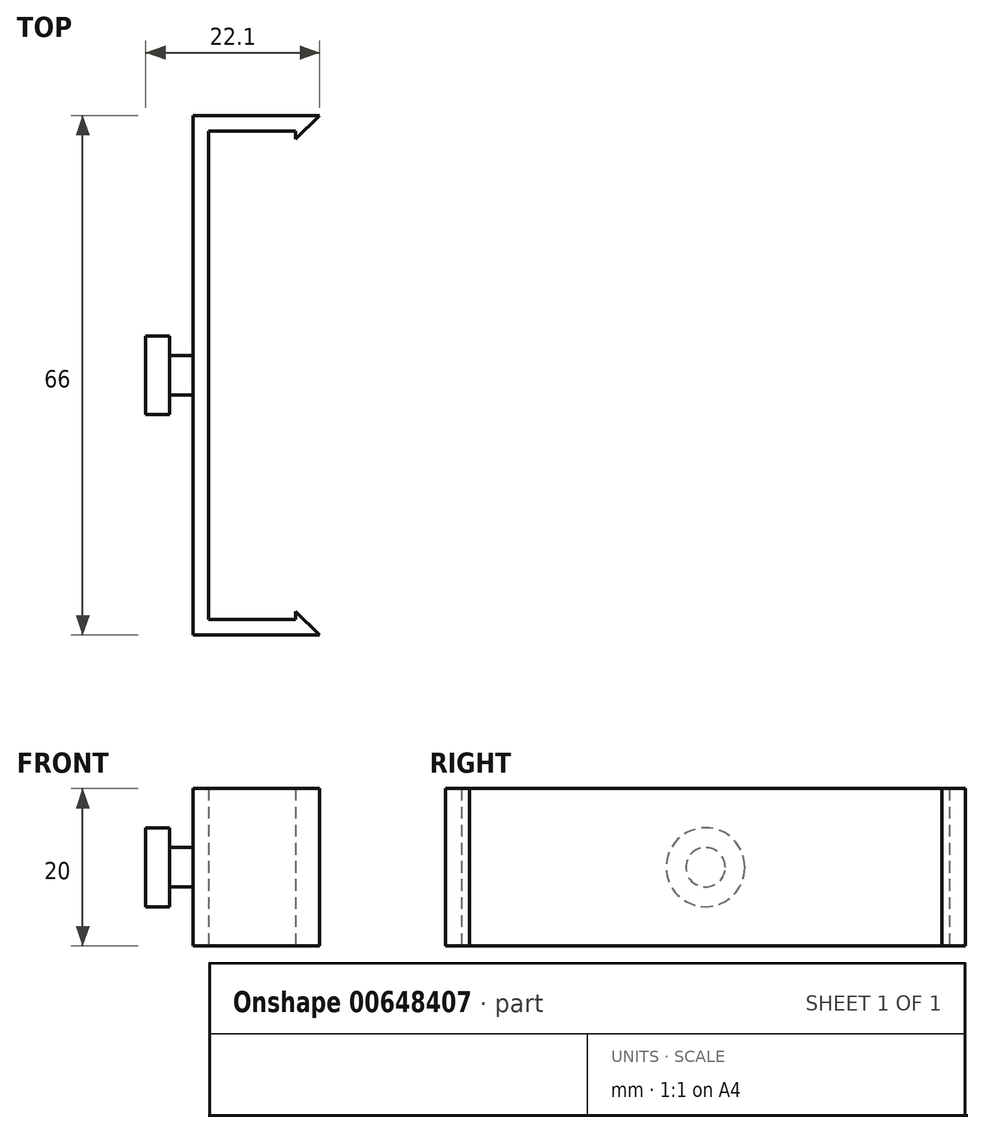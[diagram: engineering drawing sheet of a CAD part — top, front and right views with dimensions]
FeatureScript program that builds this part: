
annotation { "Feature Type Name" : "Feature", "Feature Type Description" : "" }
export const myFeature = defineFeature(function(context is Context, id is Id, definition is map)
    precondition{}
    {
        {
            var Q0;
            Q0=qCreatedBy(makeId("Top.planeOp"),FACE);
            var sketch = newSketch(context, id + "F0", { "sketchPlane" : qUnion([Q0])});
            skLineSegment(sketch, "E0", {"start": v(0.96, 0) * mm, "end": v(0.96, -33) * mm});
            skLineSegment(sketch, "E1", {"start": v(0.96, -33) * mm, "end": v(17.06, -33) * mm});
            skLineSegment(sketch, "E2", {"start": v(17.06, -33) * mm, "end": v(13.96, -30) * mm});
            skLineSegment(sketch, "E3", {"start": v(13.96, -30) * mm, "end": v(13.96, -31) * mm});
            skLineSegment(sketch, "E4", {"start": v(13.96, -31) * mm, "end": v(2.96, -31) * mm});
            skLineSegment(sketch, "E5", {"start": v(2.96, -31) * mm, "end": v(2.96, 0) * mm});
            skPoint(sketch, "E6.start.orphan", {"position": v(17.06, 48.33) * mm});
            skPoint(sketch, "E7.start.orphan", {"position": v(13.96, 44.52) * mm});
            skLineSegment(sketch, "E8.MirrorCS", {"start": v(13.96, 30) * mm, "end": v(13.96, 31) * mm});
            skLineSegment(sketch, "E9.MirrorCS", {"start": v(17.06, 33) * mm, "end": v(13.96, 30) * mm});
            skLineSegment(sketch, "E10.MirrorCS", {"start": v(13.96, 31) * mm, "end": v(2.96, 31) * mm});
            skLineSegment(sketch, "E11.MirrorCS", {"start": v(0.96, 33) * mm, "end": v(17.06, 33) * mm});
            skLineSegment(sketch, "E12.MirrorCS", {"start": v(0.96, 0) * mm, "end": v(0.96, 33) * mm});
            skLineSegment(sketch, "E13.MirrorCS", {"start": v(2.96, 31) * mm, "end": v(2.96, 0) * mm});
            skSolve(sketch);
        }
        {
            var Q0;
            Q0 = qSketchRegion(id + "F0", true);
            extrude(context, id + "F1", {"entities" : qUnion([Q0]), "depth" : 20 * mm, "offsetDistance" : 25 * mm});
        }
        {
            var Q0;
            Q0=makeQuery(id+"F1.opExtrude","SWEPT_FACE",FACE,{"disambiguationData":[OSD([sQuery(id+"F0.wireOp",EDGE,"E0"),sQuery(id+"F0.wireOp",EDGE,"E12.MirrorCS")])]});
            var sketch = newSketch(context, id + "F2", { "sketchPlane" : qUnion([Q0])});
            skLineSegment(sketch, "E14", {"start": v(0, 20) * mm, "end": v(0, 0) * mm});
            skLineSegment(sketch, "E15", {"start": v(-33, 10) * mm, "end": v(33, 10) * mm});
            skCircle(sketch, "E16", {"center": v(0, 10) * mm, "radius": 2.5 * mm});
            skSolve(sketch);
        }
        {
            var Q0;
            Q0 = qSketchRegion(id + "F2", true);
            extrude(context, id + "F3", {"entities" : qUnion([Q0]), "operationType" : NewBodyOperationType.ADD, "depth" : 3 * mm, "offsetDistance" : 25 * mm});
        }
        {
            var Q0;
            Q0=makeQuery(id+"F3.opExtrude","CAP_FACE",FACE,{"disambiguationData":[OSD([sQuery(id+"F2.wireOp",EDGE,"E16")])],"isStart":false});
            var sketch = newSketch(context, id + "F4", { "sketchPlane" : qUnion([Q0])});
            skCircle(sketch, "E17", {"center": v(0, 10) * mm, "radius": 5 * mm});
            skSolve(sketch);
        }
        {
            var Q0;
            Q0 = qSketchRegion(id + "F4", true);
            extrude(context, id + "F5", {"entities" : qUnion([Q0]), "operationType" : NewBodyOperationType.ADD, "depth" : 3 * mm, "offsetDistance" : 25 * mm});
        }
    });
